# Revit family: Mixing-Valve-Trim_Thermostatic_Transitional_Nexus_TS794C_TOTO
name_source: partatom
category: Plumbing Fixtures
revit_build: Autodesk Revit Architecture 2013 (Build: 20130531_2115(x64)
units: mm (PartAtom-declared; Revit-internal decimal feet)

## types (1)
- TS794C
    04 CSI = 22 42 13
    95 CSI = 15410
    ADA Compliant = No
    Assembly Code = D2010710
    CAD Drawing URL = http://assets.totousa.com
    CW Connection = No
    CWFU = 0
    Certifications = IAPMO(cUPC), State of Massachusetts, City of Los Angeles
    Code Compliance = UPC, IPC, NSPC, NPC Canada, and others
    Color Availability = #CP Polished Chrome, #BN Brushed Nickel, #PN Polished Nickel
    Default Elevation = 3' - 7 1/4"
    Depth = 0' - 3 1/2"
    Description = Nexus® Thermostatic Mixing Valve Trim with Single Volume Control
    Finish = Metal - TOTO - Chrome - Polished
    HW Connection = No
    HWFU = 0
    Height = 0' - 9 7/16"
    Industry Standards = Meets and exceeds ASME A112.19.2/CSA B45.1
    Manufacturer = TOTO USA, Inc.
    Manufacturer Fax = (770) 282-0002
    Material = Brass
    Model = TS794C
    Series = Nexus
    Shipping Weight = 5.50 lb
    Spec Sheet URL = http://assets.totousa.com
    Style = Transitional
    Subcategory = Mixing Valve
    Toto BIM Number = BM-00168
    URL = http://www.totousa.com
    Vent Connection = No
    WFU = 0
    Warranty = Limited Lifetime (Residential); One Year (Commercial)
    Warranty URL = http://www.totousa.com
    Waste Connection = No
    Width = 0' - 5 1/2"

## geometry (parser evidence)
native form markers: Blend x24, Sweep x1
no freeform markers — native parametric forms only
